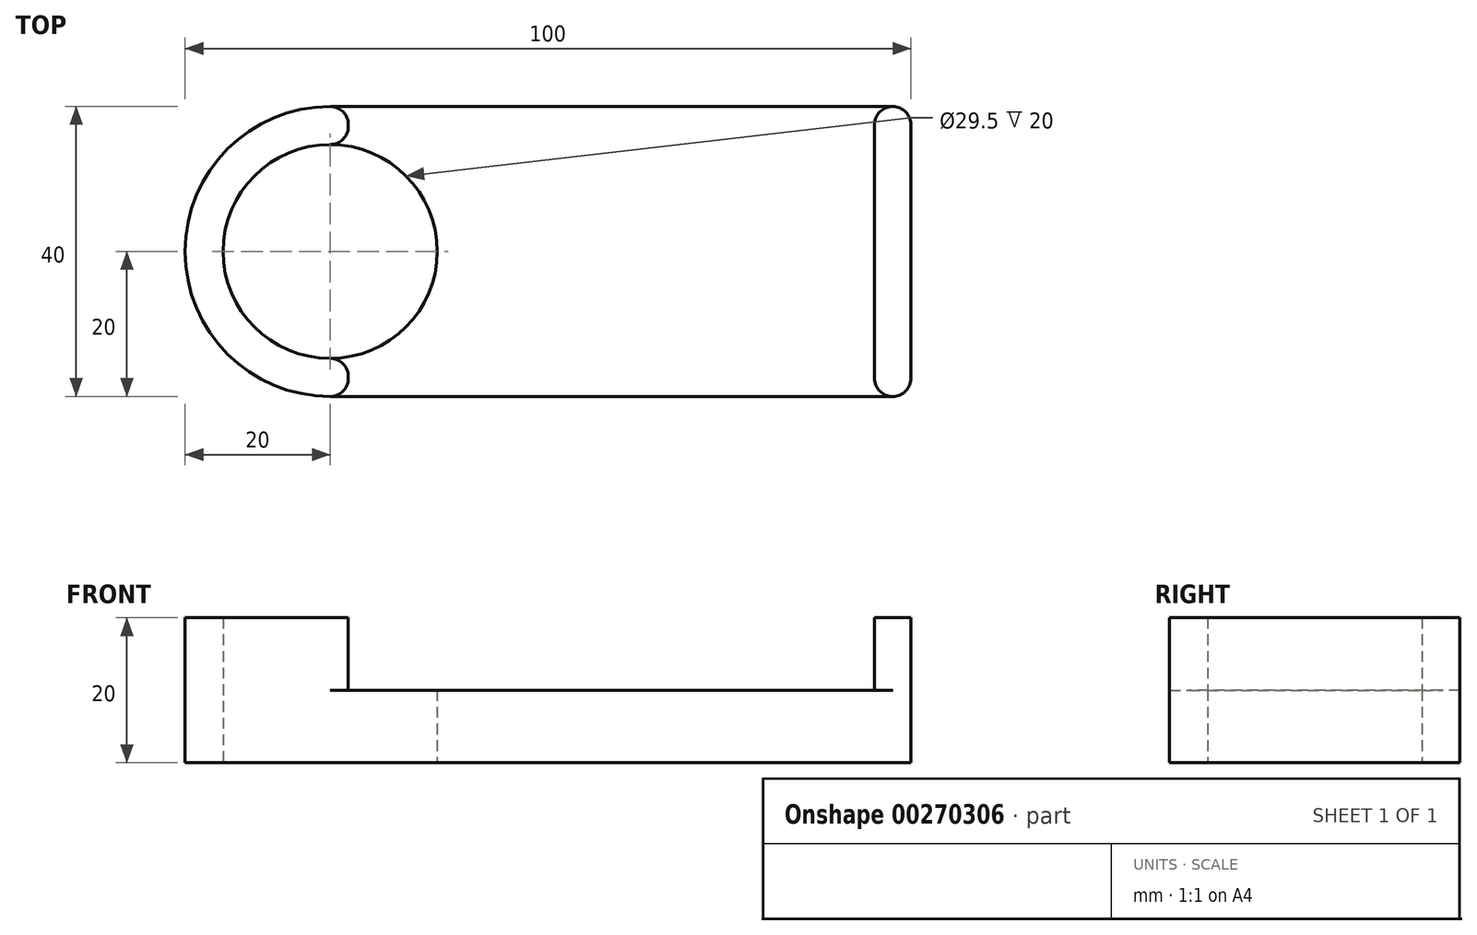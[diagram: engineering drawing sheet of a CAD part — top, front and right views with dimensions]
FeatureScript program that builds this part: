
annotation { "Feature Type Name" : "Feature", "Feature Type Description" : "" }
export const myFeature = defineFeature(function(context is Context, id is Id, definition is map)
    precondition{}
    {
        {
            var Q0;
            Q0=qCreatedBy(makeId("Top.planeOp"),FACE);
            var sketch = newSketch(context, id + "F0", { "sketchPlane" : qUnion([Q0])});
            skLineSegment(sketch, "E0.bottom", {"start": v(20, 0) * mm, "end": v(97.5, 0) * mm});
            skLineSegment(sketch, "E0.top", {"start": v(20, 40) * mm, "end": v(97.5, 40) * mm});
            skLineSegment(sketch, "E0.left", {"start": v(0, 20) * mm, "end": v(0, 20) * mm});
            skLineSegment(sketch, "E0.right", {"start": v(100, 2.5) * mm, "end": v(100, 37.5) * mm});
            skLineSegment(sketch, "E1.bottom", {"start": v(0, 0) * mm, "end": v(20, 0) * mm, "construction": true});
            skLineSegment(sketch, "E1.top", {"start": v(0, 20) * mm, "end": v(20, 20) * mm, "construction": true});
            skLineSegment(sketch, "E1.left", {"start": v(0, 0) * mm, "end": v(0, 20) * mm, "construction": true});
            skLineSegment(sketch, "E1.right", {"start": v(20, 0) * mm, "end": v(20, 20) * mm, "construction": true});
            skCircle(sketch, "E2", {"center": v(20, 20) * mm, "radius": 14.75 * mm});
            skPoint(sketch, "E3.visualSharp", {"position": v(0, 0) * mm});
            skArc(sketch, "E3.filletArc", {"start": v(0, 20) * mm, "mid": v(5.86, 5.86) * mm, "end": v(20, 0) * mm});
            skPoint(sketch, "E4.visualSharp", {"position": v(0, 40) * mm});
            skArc(sketch, "E4.filletArc", {"start": v(20, 40) * mm, "mid": v(5.86, 34.14) * mm, "end": v(0, 20) * mm});
            skPoint(sketch, "E5.visualSharp", {"position": v(100, 40) * mm});
            skArc(sketch, "E5.filletArc", {"start": v(100, 37.5) * mm, "mid": v(99.27, 39.27) * mm, "end": v(97.5, 40) * mm});
            skPoint(sketch, "E6.visualSharp", {"position": v(100, 0) * mm});
            skArc(sketch, "E6.filletArc", {"start": v(97.5, 0) * mm, "mid": v(99.27, 0.73) * mm, "end": v(100, 2.5) * mm});
            skSolve(sketch);
        }
        {
            var Q0;
            Q0=makeQuery(id+"F0.imprint","IMPRINT",FACE,{"disambiguationData":[TD([[makeQuery(id+"F0.imprint","IMPRINT",EDGE,{"derivedFrom":sQuery(id+"F0.wireOp",EDGE,"E0.bottom")}),1.0]])]});
            extrude(context, id + "F1", {"entities" : qUnion([Q0]), "depth" : 10 * mm});
        }
        {
            var Q0;
            Q0=makeQuery(id+"F1.opExtrude","CAP_FACE",FACE,{"disambiguationData":[OSD([sQuery(id+"F0.wireOp",EDGE,"E0.bottom"),sQuery(id+"F0.wireOp",EDGE,"E0.top"),sQuery(id+"F0.wireOp",EDGE,"E0.right"),sQuery(id+"F0.wireOp",EDGE,"E2"),sQuery(id+"F0.wireOp",EDGE,"E3.filletArc"),sQuery(id+"F0.wireOp",EDGE,"E4.filletArc"),sQuery(id+"F0.wireOp",EDGE,"E5.filletArc"),sQuery(id+"F0.wireOp",EDGE,"E6.filletArc")])],"isStart":false});
            var sketch = newSketch(context, id + "F2", { "sketchPlane" : qUnion([Q0])});
            skArc(sketch, "E7.0", {"start": v(20, 40) * mm, "mid": v(0, 20) * mm, "end": v(20, 0) * mm});
            skLineSegment(sketch, "E8.bottom", {"start": v(20, 40) * mm, "end": v(20, 40) * mm});
            skLineSegment(sketch, "E8.right", {"start": v(22.5, 37.5) * mm, "end": v(22.5, 37.5) * mm});
            skLineSegment(sketch, "E9.bottom", {"start": v(20, 0) * mm, "end": v(20, 0) * mm});
            skLineSegment(sketch, "E9.right", {"start": v(22.5, 2.5) * mm, "end": v(22.5, 2.5) * mm});
            skPoint(sketch, "E10.visualSharp", {"position": v(22.5, 0) * mm});
            skArc(sketch, "E10.filletArc", {"start": v(20, 0) * mm, "mid": v(21.77, 0.73) * mm, "end": v(22.5, 2.5) * mm});
            skPoint(sketch, "E11.visualSharp", {"position": v(22.5, 40) * mm});
            skArc(sketch, "E11.filletArc", {"start": v(22.5, 37.5) * mm, "mid": v(21.77, 39.27) * mm, "end": v(20, 40) * mm});
            skLineSegment(sketch, "E12", {"start": v(0, 0) * mm, "end": v(0, 20) * mm, "construction": true});
            skLineSegment(sketch, "E13", {"start": v(0, 0) * mm, "end": v(20, 0) * mm, "construction": true});
            skArc(sketch, "E14", {"start": v(20, 34.75) * mm, "mid": v(5.25, 20) * mm, "end": v(20, 5.25) * mm});
            skLineSegment(sketch, "E15", {"start": v(20, 34.75) * mm, "end": v(20, 34.75) * mm});
            skLineSegment(sketch, "E16", {"start": v(22.5, 37.25) * mm, "end": v(22.5, 37.5) * mm});
            skLineSegment(sketch, "E17", {"start": v(20, 5.25) * mm, "end": v(20, 5.25) * mm});
            skLineSegment(sketch, "E18", {"start": v(22.5, 2.75) * mm, "end": v(22.5, 2.5) * mm});
            skPoint(sketch, "E19.visualSharp", {"position": v(22.5, 5.25) * mm});
            skArc(sketch, "E19.filletArc", {"start": v(22.5, 2.75) * mm, "mid": v(21.77, 4.52) * mm, "end": v(20, 5.25) * mm});
            skPoint(sketch, "E20.visualSharp", {"position": v(22.5, 34.75) * mm});
            skArc(sketch, "E20.filletArc", {"start": v(20, 34.75) * mm, "mid": v(21.77, 35.48) * mm, "end": v(22.5, 37.25) * mm});
            skArc(sketch, "E21.0", {"start": v(100, 37.5) * mm, "mid": v(99.27, 39.27) * mm, "end": v(97.5, 40) * mm});
            skArc(sketch, "E22.0", {"start": v(97.5, 0) * mm, "mid": v(99.27, 0.73) * mm, "end": v(100, 2.5) * mm});
            skArc(sketch, "E23", {"start": v(100, 37.5) * mm, "mid": v(97.5, 40) * mm, "end": v(95, 37.5) * mm});
            skArc(sketch, "E24", {"start": v(95, 2.5) * mm, "mid": v(97.5, 0) * mm, "end": v(100, 2.5) * mm});
            skLineSegment(sketch, "E25.0", {"start": v(100, 2.5) * mm, "end": v(100, 37.5) * mm});
            skLineSegment(sketch, "E26", {"start": v(95, 37.5) * mm, "end": v(95, 2.5) * mm});
            skSolve(sketch);
        }
        {
            var Q0;
            Q0=makeQuery(id+"F2.imprint","IMPRINT",FACE,{"disambiguationData":[TD([[makeQuery(id+"F2.imprint","IMPRINT",EDGE,{"derivedFrom":sQuery(id+"F2.wireOp",EDGE,"E7.0")}),1.0]])]});
            var Q1;
            {var subQ0=sQuery(id+"F2.wireOp",EDGE,"tU6jG2RC-b3zX-LvBe-GzcY-utHJA5dh4MJE");var subQ1=makeQuery(id+"F2.imprint","INTERSECT",VERTEX,{"derivedFrom":[makeQuery(id+"F1.opExtrude","CAP_EDGE",EDGE,{"disambiguationData":[OSD([sQuery(id+"F0.wireOp",EDGE,"E0.top")])],"isStart":false}),subQ0]});Q1=makeQuery(id+"F2.imprint","IMPRINT",FACE,{"disambiguationData":[TD([[makeQuery(id+"F2.imprint","IMPRINT",EDGE,{"disambiguationData":[TD([[subQ1,1.0]])],"derivedFrom":subQ0}),1.0]])]});}
            var Q2;
            {var subQ0=sQuery(id+"F2.wireOp",EDGE,"VrWUfeW0-9n8e-DoVb-6T6y-UHncELFjFntB");var subQ1=makeQuery(id+"F2.imprint","INTERSECT",VERTEX,{"derivedFrom":[makeQuery(id+"F1.opExtrude","CAP_EDGE",EDGE,{"disambiguationData":[OSD([sQuery(id+"F0.wireOp",EDGE,"E0.bottom")])],"isStart":false}),subQ0]});Q2=makeQuery(id+"F2.imprint","IMPRINT",FACE,{"disambiguationData":[TD([[makeQuery(id+"F2.imprint","IMPRINT",EDGE,{"disambiguationData":[TD([[subQ1,1.0]])],"derivedFrom":subQ0}),1.0]])]});}
            var Q3;
            {var subQ2=sQuery(id+"F2.wireOp",EDGE,"E25.0");Q3=makeQuery(id+"F2.imprint","IMPRINT",FACE,{"disambiguationData":[TD([[makeQuery(id+"F2.imprint","IMPRINT",EDGE,{"derivedFrom":subQ2}),1.0]])]});}
            extrude(context, id + "F3", {"entities" : qUnion([Q0, Q1, Q2, Q3]), "operationType" : NewBodyOperationType.ADD, "depth" : 10 * mm});
        }
    });
